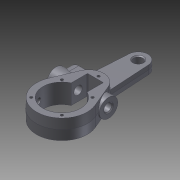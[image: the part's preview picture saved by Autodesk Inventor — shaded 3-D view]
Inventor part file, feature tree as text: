
AUTODESK INVENTOR PART (.ipt)
format: ipt  version: 2011 SP2 (Build 150309200, 309)  size: 241,664 bytes
history: native  units: mm
features: sketch x7, hole x6, extrude x5, plane x2, fillet x2, other x2, chamfer x2
ambient origin geometry x8: Origin, YZ Plane, XZ Plane, XY Plane, X Axis, Y Axis, Z Axis, Center Point
bodies: Solid1 (feature_tree)
feature tree (26):
  extrude  "Extrusion1"  Depth=25.0mm
  extrude  "Extrusion2"  Depth=32.0mm
  plane  "Work Plane1"
  extrude  "Extrusion3"  Depth=125.0mm
  extrude  "Extrusion4"  Depth=14.0mm
  fillet  "Fillet1"  Radius=37.0mm
  fillet  "Fillet2"  Radius=15.0mm
  plane  "Work Plane2"
  extrude  "Extrusion5"  Depth=86.0mm TaperAngle=0.0deg
  hole  "Hole1"  [1 undecoded]
  hole  "Hole2"  [1 undecoded]
  hole  "Hole3"  [1 undecoded]
  hole  "Hole4"  [1 undecoded]
  hole  "Hole5"  [1 undecoded]
  sketch  "Sketch7"  dims[d17=55.0mm d18=10.0mm d19=0.0mm d20=1.0mm d21=1.0mm d22=60.5mm d23=33.0mm d24=14.0mm d25=10.0mm d26=0.0mm d27=10.0mm d28=10.0mm d29=13.0mm d30=6.0mm d31=4.0mm d32=2.0mm d33=90.0deg d34=8.0mm d35=0.0mm d36=10.0mm d37=10.0mm d38=13.8mm d39=6.0mm d40=4.0mm d41=2.0mm d42=90.0deg d43=8.0mm d44=20.594885mm d45=10.0mm d46=10.0mm d47=8.917mm d48=10.0mm d49=4.0mm d50=2.0mm d51=90.0deg d52=10.0mm d53=20.594885mm d54=10.0mm d55=10.0mm d56=15.0mm d57=10.0mm d58=4.0mm d59=2.0mm d60=90.0deg d61=10.0mm d62=0.0mm d64=45.0deg d65=35.5mm d66=60.0mm d67=40.0mm d69=360.0deg d71=4.3mm d72=10.0mm d73=4.0mm d74=2.0mm d75=90.0deg d76=10.0mm d77=20.594885mm d78=15.0deg d79=10.0mm d80=10.0mm d81=8.917mm d82=10.0mm d83=4.0mm d84=2.0mm d85=90.0deg d86=10.0mm d87=0.0mm d88=1.5mm d89=2.0mm d90=45.0deg d91=1.5mm d92=2.0mm d93=45.0deg]
  other  "Work Point1"
  hole  "Hole6"  [1 undecoded]
  chamfer  "Chamfer1"  Distance=14.0mm
  chamfer  "Chamfer2"  Distance=10.0mm
  sketch  "Sketch1"  dims[d0=42.0mm d1=25.0mm]
  sketch  "Sketch2"  dims[d2=44.0mm d3=32.0mm d4=-0.349066mm]
  sketch  "Sketch3"  dims[d5=16.0mm d6=125.0mm]
  sketch  "Sketch4"  dims[d7=1.22173mm d8=14.0mm d9=-0.349066mm d10=37.0mm d11=15.0mm]
  sketch  "Sketch5"  dims[d12=39.5mm d13=86.0mm d14=0.0mm]
  sketch  "Sketch6"  dims[d15=31.0mm d16=26.0mm]
  other  "Work Axis1"
note: 6 required parameter values undecoded (feature->parameter linkage not recoverable at this tier; creation-order binding heuristic only, values carry confidence <= 0.55)
